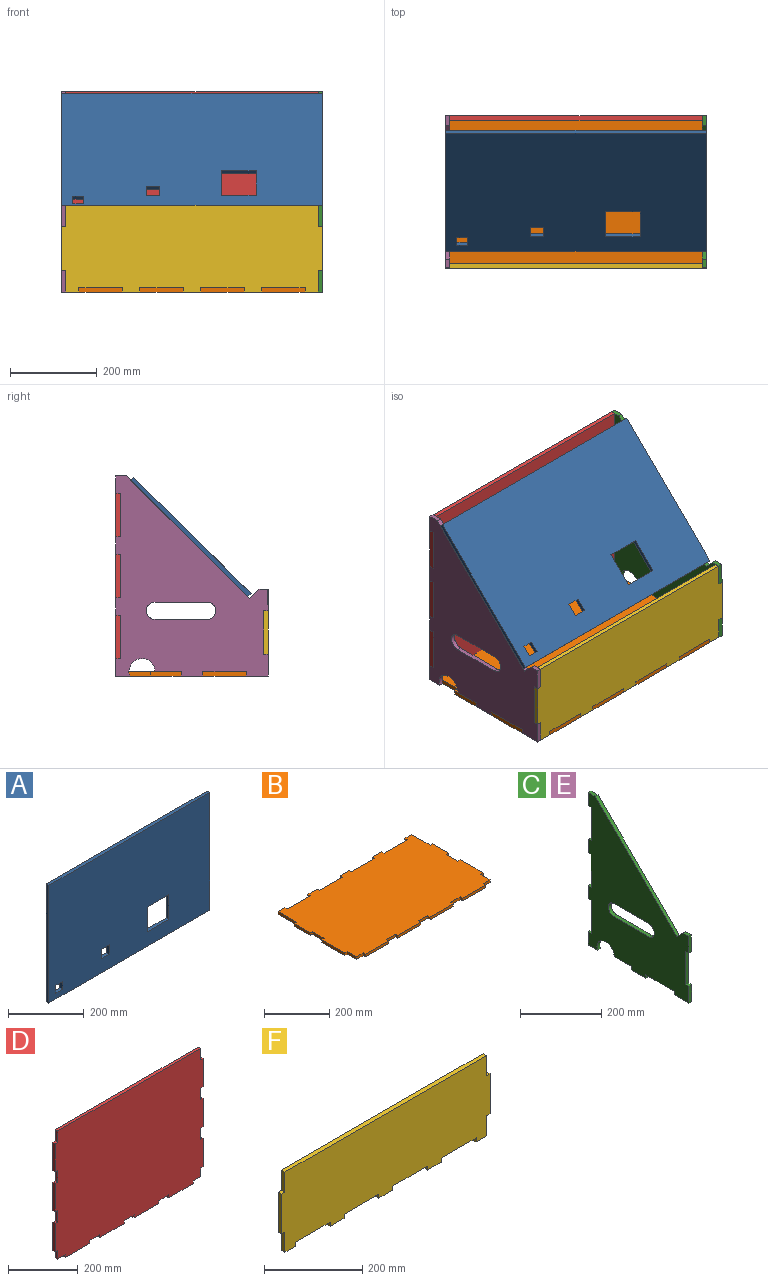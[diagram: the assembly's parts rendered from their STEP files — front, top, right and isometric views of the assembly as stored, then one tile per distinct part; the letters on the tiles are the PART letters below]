
ASSEMBLY  parts=6 mates=5
PART A: 18 faces, bbox 600x10x380 mm
  f0: plane 600x10mm, normal (0,0,1), area 6000mm2, adj f1,f15,f16,f17
  f1: plane 380x10mm, normal (-1,0,0), area 3800mm2, adj f0,f2,f16,f17
  f2: plane 600x10mm, normal (0,0,-1), area 6000mm2, adj f1,f15,f16,f17
  f3: plane 80x10mm, normal (1,0,0), area 800mm2, adj f4,f12,f16,f17
  f4: plane 80x10mm, normal (0,0,-1), area 800mm2, adj f3,f5,f16,f17
  f5: plane 80x10mm, normal (-1,0,0), area 800mm2, adj f4,f12,f16,f17
  f6: plane 30x10mm, normal (1,0,0), area 300mm2, adj f7,f13,f16,f17
  f7: plane 30x10mm, normal (0,0,-1), area 300mm2, adj f6,f8,f16,f17
  f8: plane 30x10mm, normal (-1,0,0), area 300mm2, adj f7,f13,f16,f17
  f9: plane 25x10mm, normal (1,0,0), area 250mm2, adj f10,f14,f16,f17
  f10: plane 25x10mm, normal (0,0,-1), area 250mm2, adj f9,f11,f16,f17
  f11: plane 25x10mm, normal (-1,0,0), area 250mm2, adj f10,f14,f16,f17
  f12: plane 80x10mm, normal (0,0,1), area 800mm2, adj f3,f5,f16,f17
  f13: plane 30x10mm, normal (0,0,1), area 300mm2, adj f6,f8,f16,f17
  f14: plane 25x10mm, normal (0,0,1), area 250mm2, adj f9,f11,f16,f17
  f15: plane 380x10mm, normal (1,0,0), area 3800mm2, adj f0,f2,f16,f17
  f16: plane 600x380mm, normal (0,-1,0), area 220075mm2, adj f0,f1,f2,f3,f4,f5,f6,f7
  f17: plane 600x380mm, normal (0,1,0), area 220075mm2, adj f0,f1,f2,f3,f4,f5,f6,f7
PART B: 54 faces, bbox 600x350x10 mm
  f0: plane 40x10mm, normal (0,1,0), area 400mm2, adj f1,f51,f52,f53
  f1: plane 10x10mm, normal (-1,0,0), area 100mm2, adj f0,f2,f52,f53
  f2: plane 100x10mm, normal (0,1,0), area 1000mm2, adj f1,f3,f52,f53
  f3: plane 10x10mm, normal (1,0,0), area 100mm2, adj f2,f4,f52,f53
  f4: plane 40x10mm, normal (0,1,0), area 400mm2, adj f3,f5,f52,f53
  f5: plane 10x10mm, normal (-1,0,0), area 100mm2, adj f4,f6,f52,f53
  f6: plane 100x10mm, normal (0,1,0), area 1000mm2, adj f5,f7,f52,f53
  f7: plane 10x10mm, normal (1,0,0), area 100mm2, adj f6,f8,f52,f53
  f8: plane 40x10mm, normal (0,1,0), area 400mm2, adj f7,f9,f52,f53
  f9: plane 10x10mm, normal (-1,0,0), area 100mm2, adj f8,f10,f52,f53
  f10: plane 100x10mm, normal (0,1,0), area 1000mm2, adj f9,f11,f52,f53
  f11: plane 10x10mm, normal (1,0,0), area 100mm2, adj f10,f12,f52,f53
  f12: plane 30x10mm, normal (0,1,0), area 300mm2, adj f11,f13,f52,f53
  f13: plane 80x10mm, normal (-1,0,0), area 800mm2, adj f12,f14,f52,f53
  f14: plane 10x10mm, normal (0,1,0), area 100mm2, adj f13,f15,f52,f53
  f15: plane 70x10mm, normal (-1,0,0), area 700mm2, adj f14,f16,f52,f53
  f16: plane 10x10mm, normal (0,-1,0), area 100mm2, adj f15,f17,f52,f53
  f17: plane 50x10mm, normal (-1,0,0), area 500mm2, adj f16,f18,f52,f53
  f18: plane 10x10mm, normal (0,1,0), area 100mm2, adj f17,f19,f52,f53
  f19: plane 100x10mm, normal (-1,0,0), area 1000mm2, adj f18,f20,f52,f53
  f20: plane 10x10mm, normal (0,-1,0), area 100mm2, adj f19,f21,f52,f53
  f21: plane 40x10mm, normal (-1,0,0), area 400mm2, adj f20,f22,f52,f53
  f22: plane 30x10mm, normal (0,-1,0), area 300mm2, adj f21,f23,f52,f53
  f23: plane 10x10mm, normal (-1,0,0), area 100mm2, adj f22,f24,f52,f53
  f24: plane 100x10mm, normal (0,-1,0), area 1000mm2, adj f23,f25,f52,f53
  f25: plane 10x10mm, normal (1,0,0), area 100mm2, adj f24,f26,f52,f53
  f26: plane 40x10mm, normal (0,-1,0), area 400mm2, adj f25,f27,f52,f53
  f27: plane 10x10mm, normal (-1,0,0), area 100mm2, adj f26,f28,f52,f53
  f28: plane 100x10mm, normal (0,-1,0), area 1000mm2, adj f27,f29,f52,f53
  f29: plane 10x10mm, normal (1,0,0), area 100mm2, adj f28,f30,f52,f53
  f30: plane 40x10mm, normal (0,-1,0), area 400mm2, adj f29,f31,f52,f53
  f31: plane 10x10mm, normal (-1,0,0), area 100mm2, adj f30,f32,f52,f53
  f32: plane 100x10mm, normal (0,-1,0), area 1000mm2, adj f31,f33,f52,f53
  f33: plane 10x10mm, normal (1,0,0), area 100mm2, adj f32,f34,f52,f53
  f34: plane 40x10mm, normal (0,-1,0), area 400mm2, adj f33,f35,f52,f53
  f35: plane 10x10mm, normal (-1,0,0), area 100mm2, adj f34,f36,f52,f53
  f36: plane 100x10mm, normal (0,-1,0), area 1000mm2, adj f35,f37,f52,f53
  f37: plane 10x10mm, normal (1,0,0), area 100mm2, adj f36,f38,f52,f53
  f38: plane 30x10mm, normal (0,-1,0), area 300mm2, adj f37,f39,f52,f53
  f39: plane 40x10mm, normal (1,0,0), area 400mm2, adj f38,f40,f52,f53
  f40: plane 10x10mm, normal (0,-1,0), area 100mm2, adj f39,f41,f52,f53
  f41: plane 100x10mm, normal (1,0,0), area 1000mm2, adj f40,f42,f52,f53
  f42: plane 10x10mm, normal (0,1,0), area 100mm2, adj f41,f43,f52,f53
  f43: plane 50x10mm, normal (1,0,0), area 500mm2, adj f42,f44,f52,f53
  f44: plane 10x10mm, normal (0,-1,0), area 100mm2, adj f43,f45,f52,f53
  f45: plane 70x10mm, normal (1,0,0), area 700mm2, adj f44,f46,f52,f53
  f46: plane 10x10mm, normal (0,1,0), area 100mm2, adj f45,f47,f52,f53
  f47: plane 80x10mm, normal (1,0,0), area 800mm2, adj f46,f48,f52,f53
  f48: plane 30x10mm, normal (0,1,0), area 300mm2, adj f47,f49,f52,f53
  f49: plane 10x10mm, normal (-1,0,0), area 100mm2, adj f48,f50,f52,f53
  f50: plane 100x10mm, normal (0,1,0), area 1000mm2, adj f49,f51,f52,f53
  f51: plane 10x10mm, normal (1,0,0), area 100mm2, adj f0,f50,f52,f53
  f52: plane 600x350mm, normal (0,0,1), area 200600mm2, adj f0,f1,f2,f3,f4,f5,f6,f7
  f53: plane 600x350mm, normal (0,0,-1), area 200600mm2, adj f0,f1,f2,f3,f4,f5,f6,f7
PART C: 37 faces, bbox 10x350x460 mm
  f0: cylinder r=30mm len=60mm, axis (-1,0,0), area 1044.4mm2, adj f1,f34,f35,f36
  f1: plane 31.72x10mm, normal (0,0,-1), area 317.2mm2, adj f0,f2,f35,f36
  f2: plane 40x10mm, normal (0,1,0), area 400mm2, adj f1,f3,f35,f36
  f3: plane 10x10mm, normal (0,0,1), area 100mm2, adj f2,f4,f35,f36
  f4: plane 100x10mm, normal (0,1,0), area 1000mm2, adj f3,f5,f35,f36
  f5: plane 10x10mm, normal (0,0,-1), area 100mm2, adj f4,f6,f35,f36
  f6: plane 40x10mm, normal (0,1,0), area 400mm2, adj f5,f7,f35,f36
  f7: plane 10x10mm, normal (0,0,1), area 100mm2, adj f6,f8,f35,f36
  f8: plane 100x10mm, normal (0,1,0), area 1000mm2, adj f7,f9,f35,f36
  f9: plane 10x10mm, normal (0,0,-1), area 100mm2, adj f8,f10,f35,f36
  f10: plane 40x10mm, normal (0,1,0), area 400mm2, adj f9,f11,f35,f36
  f11: plane 10x10mm, normal (0,0,1), area 100mm2, adj f10,f12,f35,f36
  f12: plane 100x10mm, normal (0,1,0), area 1000mm2, adj f11,f13,f35,f36
  f13: plane 10x10mm, normal (0,0,-1), area 100mm2, adj f12,f14,f35,f36
  f14: plane 40x10mm, normal (0,1,0), area 400mm2, adj f13,f15,f35,f36
  f15: plane 23.61x10mm, normal (0,0,1), area 236.1mm2, adj f14,f16,f35,f36
  f16: plane 284.34x281.33mm, normal (0,-0.7,0.71), area 4000mm2, adj f15,f17,f35,f36
  f17: plane 21.33x21.1mm, normal (0,0.71,0.7), area 300mm2, adj f16,f18,f35,f36
  f18: plane 20x10mm, normal (0,0,1), area 200mm2, adj f17,f19,f35,f36
  f19: plane 49.99x10mm, normal (0,-1,0.02), area 500mm2, adj f18,f20,f35,f36
  f20: plane 10x10mm, normal (0,0,-1), area 100mm2, adj f19,f21,f35,f36
  f21: plane 100x10mm, normal (0,-1,0), area 1000mm2, adj f20,f22,f35,f36
  f22: plane 10x10mm, normal (0,0,1), area 100mm2, adj f21,f23,f35,f36
  f23: plane 50x10mm, normal (0,-1,0), area 500mm2, adj f22,f24,f35,f36
  f24: plane 50x10mm, normal (0,0,-1), area 500mm2, adj f23,f25,f35,f36
  f25: plane 10x10mm, normal (0,1,0), area 100mm2, adj f24,f26,f35,f36
  f26: plane 100x10mm, normal (0,0,-1), area 1000mm2, adj f25,f27,f35,f36
  f27: plane 10x10mm, normal (0,-1,0), area 100mm2, adj f26,f28,f35,f36
  f28: plane 50x10mm, normal (0,0,-1), area 500mm2, adj f27,f29,f35,f36
  f29: plane 10x10mm, normal (0,1,0), area 100mm2, adj f28,f34,f35,f36
  f30: cylinder r=20mm len=40mm, axis (-1,0,0), area 628.3mm2, adj f31,f33,f35,f36
  f31: plane 120x10mm, normal (0,0,-1), area 1200mm2, adj f30,f32,f35,f36
  f32: cylinder r=20mm len=40mm, axis (-1,0,0), area 628.3mm2, adj f31,f33,f35,f36
  f33: plane 120x10mm, normal (0,0,1), area 1200mm2, adj f30,f32,f35,f36
  f34: plane 60x10mm, normal (0,0,-1), area 600mm2, adj f0,f29,f35,f36
  f35: plane 460x350mm, normal (1,0,0), area 96157.1mm2, adj f0,f1,f2,f3,f4,f5,f6,f7
  f36: plane 460x350mm, normal (-1,0,0), area 96157.1mm2, adj f0,f1,f2,f3,f4,f5,f6,f7
PART D: 46 faces, bbox 600x10x460 mm
  f0: plane 40x10mm, normal (0,0,-1), area 400mm2, adj f1,f43,f44,f45
  f1: plane 10x10mm, normal (-1,0,0), area 100mm2, adj f0,f2,f44,f45
  f2: plane 100x10mm, normal (0,0,-1), area 1000mm2, adj f1,f3,f44,f45
  f3: plane 10x10mm, normal (1,0,0), area 100mm2, adj f2,f4,f44,f45
  f4: plane 40x10mm, normal (0,0,-1), area 400mm2, adj f3,f5,f44,f45
  f5: plane 10x10mm, normal (-1,0,0), area 100mm2, adj f4,f6,f44,f45
  f6: plane 100x10mm, normal (0,0,-1), area 1000mm2, adj f5,f7,f44,f45
  f7: plane 10x10mm, normal (1,0,0), area 100mm2, adj f6,f8,f44,f45
  f8: plane 30x10mm, normal (0,0,-1), area 300mm2, adj f7,f9,f44,f45
  f9: plane 30x10mm, normal (1,0,0), area 300mm2, adj f8,f10,f44,f45
  f10: plane 10x10mm, normal (0,0,-1), area 100mm2, adj f9,f11,f44,f45
  f11: plane 100x10mm, normal (1,0,0), area 1000mm2, adj f10,f12,f44,f45
  f12: plane 10x10mm, normal (0,0,1), area 100mm2, adj f11,f13,f44,f45
  f13: plane 40x10mm, normal (1,0,0), area 400mm2, adj f12,f14,f44,f45
  f14: plane 10x10mm, normal (0,0,-1), area 100mm2, adj f13,f15,f44,f45
  f15: plane 100x10mm, normal (1,0,0), area 1000mm2, adj f14,f16,f44,f45
  f16: plane 10x10mm, normal (0,0,1), area 100mm2, adj f15,f17,f44,f45
  f17: plane 40x10mm, normal (1,0,0), area 400mm2, adj f16,f18,f44,f45
  f18: plane 10x10mm, normal (0,0,-1), area 100mm2, adj f17,f19,f44,f45
  f19: plane 100x10mm, normal (1,0,0), area 1000mm2, adj f18,f20,f44,f45
  f20: plane 10x10mm, normal (0,0,1), area 100mm2, adj f19,f21,f44,f45
  f21: plane 40x10mm, normal (1,0,0), area 400mm2, adj f20,f22,f44,f45
  f22: plane 580x10mm, normal (0,0,1), area 5800mm2, adj f21,f23,f44,f45
  f23: plane 40x10mm, normal (-1,0,0), area 400mm2, adj f22,f24,f44,f45
  f24: plane 10x10mm, normal (0,0,1), area 100mm2, adj f23,f25,f44,f45
  f25: plane 100x10mm, normal (-1,0,0), area 1000mm2, adj f24,f26,f44,f45
  f26: plane 10x10mm, normal (0,0,-1), area 100mm2, adj f25,f27,f44,f45
  f27: plane 40x10mm, normal (-1,0,0), area 400mm2, adj f26,f28,f44,f45
  f28: plane 10x10mm, normal (0,0,1), area 100mm2, adj f27,f29,f44,f45
  f29: plane 100x10mm, normal (-1,0,0), area 1000mm2, adj f28,f30,f44,f45
  f30: plane 10x10mm, normal (0,0,-1), area 100mm2, adj f29,f31,f44,f45
  f31: plane 40x10mm, normal (-1,0,0), area 400mm2, adj f30,f32,f44,f45
  f32: plane 10x10mm, normal (0,0,1), area 100mm2, adj f31,f33,f44,f45
  f33: plane 100x10mm, normal (-1,0,0), area 1000mm2, adj f32,f34,f44,f45
  f34: plane 10x10mm, normal (0,0,-1), area 100mm2, adj f33,f35,f44,f45
  f35: plane 30x10mm, normal (-1,0,0), area 300mm2, adj f34,f36,f44,f45
  f36: plane 30x10mm, normal (0,0,-1), area 300mm2, adj f35,f37,f44,f45
  f37: plane 10x10mm, normal (-1,0,0), area 100mm2, adj f36,f38,f44,f45
  f38: plane 100x10mm, normal (0,0,-1), area 1000mm2, adj f37,f39,f44,f45
  f39: plane 10x10mm, normal (1,0,0), area 100mm2, adj f38,f40,f44,f45
  f40: plane 40x10mm, normal (0,0,-1), area 400mm2, adj f39,f41,f44,f45
  f41: plane 10x10mm, normal (-1,0,0), area 100mm2, adj f40,f42,f44,f45
  f42: plane 100x10mm, normal (0,0,-1), area 1000mm2, adj f41,f43,f44,f45
  f43: plane 10x10mm, normal (1,0,0), area 100mm2, adj f0,f42,f44,f45
  f44: plane 600x460mm, normal (0,-1,0), area 271000mm2, adj f0,f1,f2,f3,f4,f5,f6,f7
  f45: plane 600x460mm, normal (0,1,0), area 271000mm2, adj f0,f1,f2,f3,f4,f5,f6,f7
PART E: same geometry as C
PART F: 30 faces, bbox 600x10x200 mm
  f0: plane 10x10mm, normal (-1,0,0), area 100mm2, adj f1,f27,f28,f29
  f1: plane 40x10mm, normal (0,0,-1), area 400mm2, adj f0,f2,f28,f29
  f2: plane 10x10mm, normal (1,0,0), area 100mm2, adj f1,f3,f28,f29
  f3: plane 100x10mm, normal (0,0,-1), area 1000mm2, adj f2,f4,f28,f29
  f4: plane 10x10mm, normal (-1,0,0), area 100mm2, adj f3,f5,f28,f29
  f5: plane 40x10mm, normal (0,0,-1), area 400mm2, adj f4,f6,f28,f29
  f6: plane 10x10mm, normal (1,0,0), area 100mm2, adj f5,f7,f28,f29
  f7: plane 100x10mm, normal (0,0,-1), area 1000mm2, adj f6,f8,f28,f29
  f8: plane 10x10mm, normal (-1,0,0), area 100mm2, adj f7,f9,f28,f29
  f9: plane 30x10mm, normal (0,0,-1), area 300mm2, adj f8,f10,f28,f29
  f10: plane 50x10mm, normal (1,0,0), area 500mm2, adj f9,f11,f28,f29
  f11: plane 10x10mm, normal (0,0,-1), area 100mm2, adj f10,f12,f28,f29
  f12: plane 100x10mm, normal (1,0,0), area 1000mm2, adj f11,f13,f28,f29
  f13: plane 10x10mm, normal (0,0,1), area 100mm2, adj f12,f14,f28,f29
  f14: plane 50x10mm, normal (1,0,0), area 500mm2, adj f13,f15,f28,f29
  f15: plane 580x10mm, normal (0,0,1), area 5800mm2, adj f14,f16,f28,f29
  f16: plane 50x10mm, normal (-1,0,0), area 500mm2, adj f15,f17,f28,f29
  f17: plane 10x10mm, normal (0,0,1), area 100mm2, adj f16,f18,f28,f29
  f18: plane 100x10mm, normal (-1,0,0), area 1000mm2, adj f17,f19,f28,f29
  f19: plane 10x10mm, normal (0,0,-1), area 100mm2, adj f18,f20,f28,f29
  f20: plane 50x10mm, normal (-1,0,0), area 500mm2, adj f19,f21,f28,f29
  f21: plane 30x10mm, normal (0,0,-1), area 300mm2, adj f20,f22,f28,f29
  f22: plane 10x10mm, normal (1,0,0), area 100mm2, adj f21,f23,f28,f29
  f23: plane 100x10mm, normal (0,0,-1), area 1000mm2, adj f22,f24,f28,f29
  f24: plane 10x10mm, normal (-1,0,0), area 100mm2, adj f23,f25,f28,f29
  f25: plane 40x10mm, normal (0,0,-1), area 400mm2, adj f24,f26,f28,f29
  f26: plane 10x10mm, normal (1,0,0), area 100mm2, adj f25,f27,f28,f29
  f27: plane 100x10mm, normal (0,0,-1), area 1000mm2, adj f0,f26,f28,f29
  f28: plane 600x200mm, normal (0,-1,0), area 114000mm2, adj f0,f1,f2,f3,f4,f5,f6,f7
  f29: plane 600x200mm, normal (0,1,0), area 114000mm2, adj f0,f1,f2,f3,f4,f5,f6,f7
PLACE A rot(axis=(-1,0,0),45.3deg) t=(-15.05,66.51,286.58)mm
PLACE B t=(0,96,-81)mm fixed
PLACE C t=(265.27,-5.67,-39.48)mm
PLACE D t=(-4.73,183.53,220.05)mm
PLACE E t=(-324.73,-5.67,-39.48)mm
PLACE F t=(-18.26,-156.47,40.5)mm
MATE fastened F.f29 <-> B.f30  axis (0,1,0) through (-24.73,-156.47,-81)mm
MATE fastened D.f45 <-> B.f4  axis (0,1,0) through (-24.73,183.53,-71)mm
MATE fastened C.f36 <-> B.f43  axis (-1,0,0) through (265.27,8.53,-81)mm
MATE fastened A.f17 <-> E.f16  axis (0,0.7,-0.71) through (-26.73,17.75,238.33)mm
MATE fastened E.f35 <-> B.f17  axis (1,0,0) through (-314.73,8.53,-81)mm
